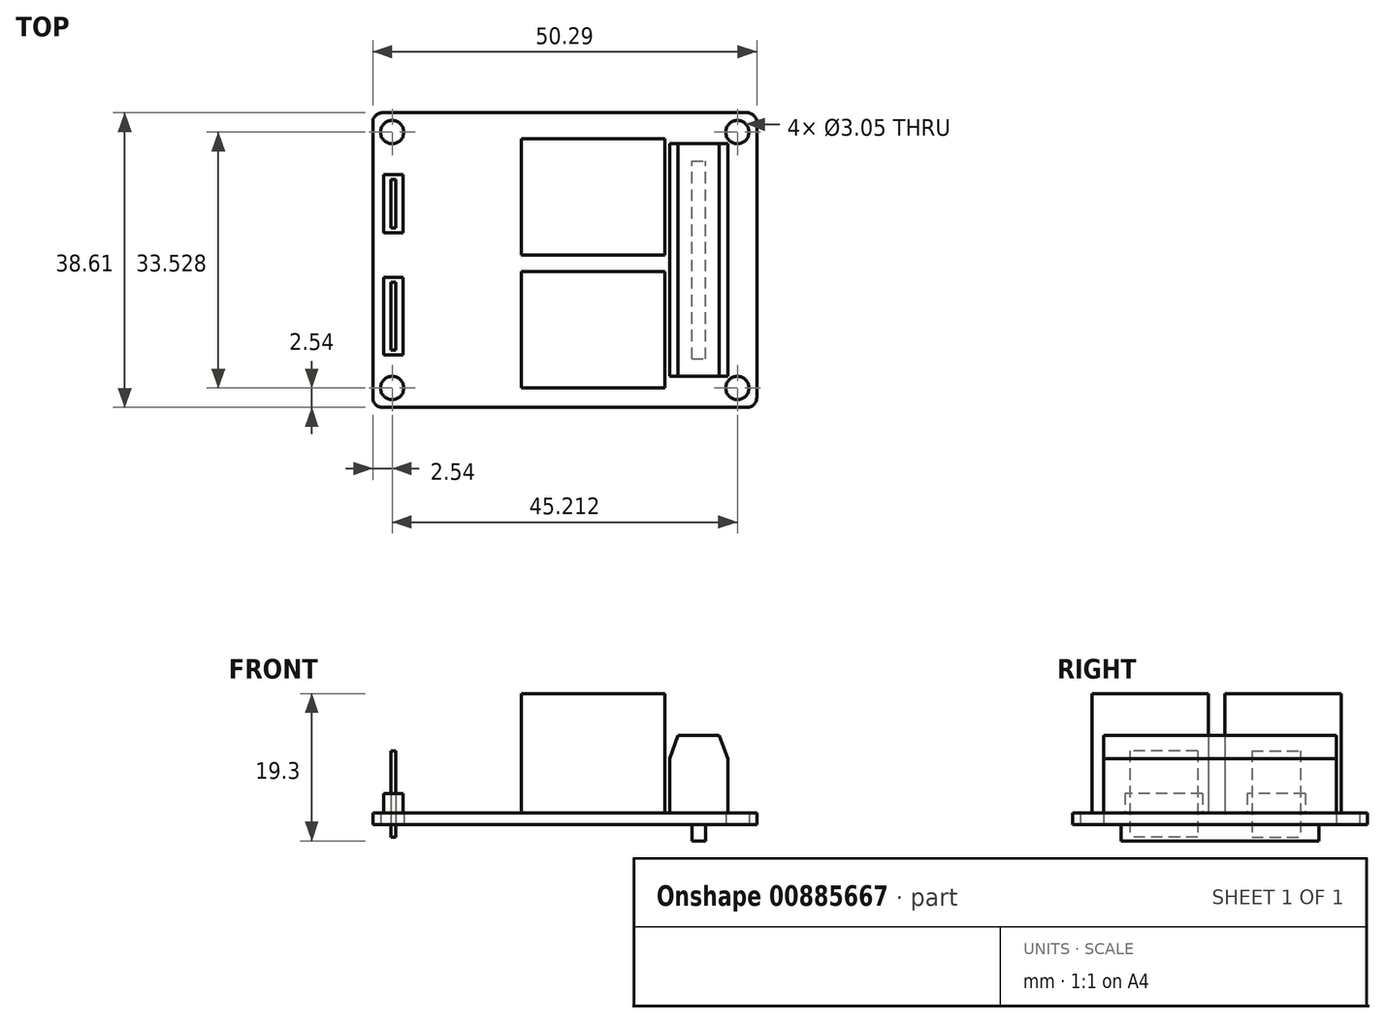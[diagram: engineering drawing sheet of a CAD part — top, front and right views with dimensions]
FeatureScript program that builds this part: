
annotation { "Feature Type Name" : "Feature", "Feature Type Description" : "" }
export const myFeature = defineFeature(function(context is Context, id is Id, definition is map)
    precondition{}
    {
        {
            var Q0;
            Q0=qCreatedBy(makeId("Top.planeOp"),FACE);
            var sketch = newSketch(context, id + "F0", { "sketchPlane" : qUnion([Q0])});
            skLineSegment(sketch, "E0.bottom", {"start": v(0, 0) * mm, "end": v(50.3, 0) * mm});
            skLineSegment(sketch, "E0.top", {"start": v(0, 38.6) * mm, "end": v(50.3, 38.6) * mm});
            skLineSegment(sketch, "E0.left", {"start": v(0, 0) * mm, "end": v(0, 38.6) * mm});
            skLineSegment(sketch, "E0.right", {"start": v(50.3, 0) * mm, "end": v(50.3, 38.6) * mm});
            skLineSegment(sketch, "E1", {"start": v(2.54, -3.55) * mm, "end": v(2.54, 40.4) * mm, "construction": true});
            skLineSegment(sketch, "E2", {"start": v(47.75, 40.69) * mm, "end": v(47.75, -3.26) * mm, "construction": true});
            skLineSegment(sketch, "E3", {"start": v(-3, 36.07) * mm, "end": v(53.81, 36.07) * mm, "construction": true});
            skLineSegment(sketch, "E4", {"start": v(-2.7, 2.54) * mm, "end": v(54.11, 2.54) * mm, "construction": true});
            skCircle(sketch, "E5", {"center": v(2.54, 36.07) * mm, "radius": 1.52 * mm});
            skCircle(sketch, "E6", {"center": v(47.75, 36.07) * mm, "radius": 1.52 * mm});
            skCircle(sketch, "E7", {"center": v(47.75, 2.54) * mm, "radius": 1.52 * mm});
            skCircle(sketch, "E8", {"center": v(2.54, 2.54) * mm, "radius": 1.52 * mm});
            skPoint(sketch, "E9.visualSharp", {"position": v(0, 38.6) * mm});
            skLineSegment(sketch, "E9.filletArc", {"start": v(0, 38.6) * mm, "end": v(0, 38.6) * mm});
            skPoint(sketch, "E10.visualSharp", {"position": v(50.3, 38.6) * mm});
            skLineSegment(sketch, "E10.filletArc", {"start": v(50.3, 38.6) * mm, "end": v(50.3, 38.6) * mm});
            skPoint(sketch, "E11.visualSharp", {"position": v(50.3, 0) * mm});
            skLineSegment(sketch, "E11.filletArc", {"start": v(50.3, 0) * mm, "end": v(50.3, 0) * mm});
            skPoint(sketch, "E12.visualSharp", {"position": v(0, 0) * mm});
            skLineSegment(sketch, "E12.filletArc", {"start": v(0, 0) * mm, "end": v(0, 0) * mm});
            skSolve(sketch);
        }
        {
            var Q0;
            Q0=makeQuery(id+"F0.imprint","IMPRINT",FACE,{"disambiguationData":[TD([[makeQuery(id+"F0.imprint","IMPRINT",EDGE,{"derivedFrom":sQuery(id+"F0.wireOp",EDGE,"E0.bottom")}),1.0]])]});
            extrude(context, id + "F1", {"entities" : qUnion([Q0]), "depth" : 1.52 * mm, "offsetDistance" : 25.4 * mm});
        }
        {
            var Q0;
            Q0=makeQuery(id+"F1.opExtrude","SWEPT_EDGE",EDGE,{"disambiguationData":[OSD([sQuery(id+"F0.wireOp",EDGE,"E0.top"),sQuery(id+"F0.wireOp",EDGE,"E0.right")])]});
            var Q1;
            Q1=makeQuery(id+"F1.opExtrude","SWEPT_EDGE",EDGE,{"disambiguationData":[OSD([sQuery(id+"F0.wireOp",EDGE,"E0.top"),sQuery(id+"F0.wireOp",EDGE,"E0.left")])]});
            var Q2;
            Q2=makeQuery(id+"F1.opExtrude","SWEPT_EDGE",EDGE,{"disambiguationData":[OSD([sQuery(id+"F0.wireOp",EDGE,"E0.bottom"),sQuery(id+"F0.wireOp",EDGE,"E0.left")])]});
            var Q3;
            Q3=makeQuery(id+"F1.opExtrude","SWEPT_EDGE",EDGE,{"disambiguationData":[OSD([sQuery(id+"F0.wireOp",EDGE,"E0.bottom"),sQuery(id+"F0.wireOp",EDGE,"E0.right")])]});
            fillet(context, id + "F2", {"entities" : qUnion([Q0, Q1, Q2, Q3]), "radius" : 1.27 * mm, "tangentPropagation" : true, "allowEdgeOverflow" : false});
        }
        {
            var Q0;
            Q0=makeQuery(id+"F1.opExtrude","CAP_FACE",FACE,{"disambiguationData":[OSD([sQuery(id+"F0.wireOp",EDGE,"E0.bottom"),sQuery(id+"F0.wireOp",EDGE,"E0.top"),sQuery(id+"F0.wireOp",EDGE,"E0.left"),sQuery(id+"F0.wireOp",EDGE,"E0.right"),sQuery(id+"F0.wireOp",EDGE,"E5"),sQuery(id+"F0.wireOp",EDGE,"E6"),sQuery(id+"F0.wireOp",EDGE,"E7"),sQuery(id+"F0.wireOp",EDGE,"E8"),sQuery(id+"F0.wireOp",EDGE,"E9.filletArc"),sQuery(id+"F0.wireOp",EDGE,"E10.filletArc"),sQuery(id+"F0.wireOp",EDGE,"E11.filletArc"),sQuery(id+"F0.wireOp",EDGE,"E12.filletArc")])],"isStart":false});
            var sketch = newSketch(context, id + "F3", { "sketchPlane" : qUnion([Q0])});
            skLineSegment(sketch, "E13.bottom", {"start": v(38.86, 34.54) * mm, "end": v(46.48, 34.54) * mm});
            skLineSegment(sketch, "E13.top", {"start": v(38.86, 4.06) * mm, "end": v(46.48, 4.06) * mm});
            skLineSegment(sketch, "E13.left", {"start": v(38.86, 34.54) * mm, "end": v(38.86, 4.06) * mm});
            skLineSegment(sketch, "E13.right", {"start": v(46.48, 34.54) * mm, "end": v(46.48, 4.06) * mm});
            skLineSegment(sketch, "E14.bottom", {"start": v(19.43, 35.18) * mm, "end": v(38.23, 35.18) * mm});
            skLineSegment(sketch, "E14.top", {"start": v(19.43, 19.94) * mm, "end": v(38.23, 19.94) * mm});
            skLineSegment(sketch, "E14.left", {"start": v(19.43, 35.18) * mm, "end": v(19.43, 19.94) * mm});
            skLineSegment(sketch, "E14.right", {"start": v(38.23, 35.18) * mm, "end": v(38.23, 19.94) * mm});
            skLineSegment(sketch, "E15.bottom", {"start": v(19.43, 17.78) * mm, "end": v(38.23, 17.78) * mm});
            skLineSegment(sketch, "E15.top", {"start": v(19.43, 2.54) * mm, "end": v(38.23, 2.54) * mm});
            skLineSegment(sketch, "E15.left", {"start": v(19.43, 17.78) * mm, "end": v(19.43, 2.54) * mm});
            skLineSegment(sketch, "E15.right", {"start": v(38.23, 17.78) * mm, "end": v(38.23, 2.54) * mm});
            skLineSegment(sketch, "E16.bottom", {"start": v(1.4, 17.02) * mm, "end": v(3.94, 17.02) * mm});
            skLineSegment(sketch, "E16.top", {"start": v(1.4, 6.86) * mm, "end": v(3.94, 6.86) * mm});
            skLineSegment(sketch, "E16.left", {"start": v(1.4, 17.02) * mm, "end": v(1.4, 6.86) * mm});
            skLineSegment(sketch, "E16.right", {"start": v(3.94, 17.02) * mm, "end": v(3.94, 6.86) * mm});
            skLineSegment(sketch, "E17.bottom", {"start": v(1.4, 30.48) * mm, "end": v(3.94, 30.48) * mm});
            skLineSegment(sketch, "E17.top", {"start": v(1.4, 22.86) * mm, "end": v(3.94, 22.86) * mm});
            skLineSegment(sketch, "E17.left", {"start": v(1.4, 30.48) * mm, "end": v(1.4, 22.86) * mm});
            skLineSegment(sketch, "E17.right", {"start": v(3.94, 30.48) * mm, "end": v(3.94, 22.86) * mm});
            skSolve(sketch);
        }
        {
            var Q0;
            Q0=makeQuery(id+"F3.imprint","IMPRINT",FACE,{"disambiguationData":[TD([[makeQuery(id+"F3.imprint","IMPRINT",EDGE,{"derivedFrom":sQuery(id+"F3.wireOp",EDGE,"E13.bottom")}),-1.0]])]});
            extrude(context, id + "F4", {"entities" : qUnion([Q0]), "depth" : 10.16 * mm, "offsetDistance" : 25.4 * mm});
        }
        {
            var Q0;
            Q0=makeQuery(id+"F4.opExtrude","CAP_EDGE",EDGE,{"disambiguationData":[OSD([sQuery(id+"F3.wireOp",EDGE,"E13.right")])],"isStart":false});
            var Q1;
            Q1=makeQuery(id+"F4.opExtrude","CAP_EDGE",EDGE,{"disambiguationData":[OSD([sQuery(id+"F3.wireOp",EDGE,"E13.left")])],"isStart":false});
            chamfer(context, id + "F5", {"entities" : qUnion([Q0, Q1]), "chamferType" : ChamferType.OFFSET_ANGLE, "width" : 3.05 * mm, "oppositeDirection" : false, "angle" : 20 * degree, "tangentPropagation" : true});
        }
        {
            var Q0;
            Q0=makeQuery(id+"F3.imprint","IMPRINT",FACE,{"disambiguationData":[TD([[makeQuery(id+"F3.imprint","IMPRINT",EDGE,{"derivedFrom":sQuery(id+"F3.wireOp",EDGE,"E14.bottom")}),-1.0]])]});
            var Q1;
            Q1=makeQuery(id+"F3.imprint","IMPRINT",FACE,{"disambiguationData":[TD([[makeQuery(id+"F3.imprint","IMPRINT",EDGE,{"derivedFrom":sQuery(id+"F3.wireOp",EDGE,"E15.bottom")}),-1.0]])]});
            extrude(context, id + "F6", {"entities" : qUnion([Q0, Q1]), "depth" : 15.62 * mm, "offsetDistance" : 25.4 * mm});
        }
        {
            var Q0;
            Q0=makeQuery(id+"F3.imprint","IMPRINT",FACE,{"disambiguationData":[TD([[makeQuery(id+"F3.imprint","IMPRINT",EDGE,{"derivedFrom":sQuery(id+"F3.wireOp",EDGE,"E17.bottom")}),-1.0]])]});
            var Q1;
            Q1=makeQuery(id+"F3.imprint","IMPRINT",FACE,{"disambiguationData":[TD([[makeQuery(id+"F3.imprint","IMPRINT",EDGE,{"derivedFrom":sQuery(id+"F3.wireOp",EDGE,"E16.bottom")}),-1.0]])]});
            extrude(context, id + "F7", {"entities" : qUnion([Q0, Q1]), "depth" : 2.54 * mm, "offsetDistance" : 25.4 * mm});
        }
        {
            var Q0;
            Q0=makeQuery(id+"F7.opExtrude","CAP_FACE",FACE,{"disambiguationData":[OSD([sQuery(id+"F3.wireOp",EDGE,"E17.bottom"),sQuery(id+"F3.wireOp",EDGE,"E17.top"),sQuery(id+"F3.wireOp",EDGE,"E17.left"),sQuery(id+"F3.wireOp",EDGE,"E17.right")])],"isStart":false});
            var sketch = newSketch(context, id + "F8", { "sketchPlane" : qUnion([Q0])});
            skLineSegment(sketch, "E18", {"start": v(2.67, 9.13) * mm, "end": v(2.67, 30.48) * mm, "construction": true});
            skLineSegment(sketch, "E19", {"start": v(2.67, 9.13) * mm, "end": v(2.67, 5.86) * mm, "construction": true});
            skLineSegment(sketch, "E20.bottom", {"start": v(2.35, 16.38) * mm, "end": v(2.98, 16.38) * mm});
            skLineSegment(sketch, "E20.top", {"start": v(2.35, 7.5) * mm, "end": v(2.98, 7.5) * mm});
            skLineSegment(sketch, "E20.left", {"start": v(2.35, 16.38) * mm, "end": v(2.35, 7.5) * mm});
            skLineSegment(sketch, "E20.right", {"start": v(2.98, 16.38) * mm, "end": v(2.98, 7.5) * mm});
            skPoint(sketch, "E21", {"position": v(2.67, 7.5) * mm});
            skLineSegment(sketch, "E22.bottom", {"start": v(2.98, 23.5) * mm, "end": v(2.35, 23.5) * mm});
            skLineSegment(sketch, "E22.top", {"start": v(2.98, 29.84) * mm, "end": v(2.35, 29.84) * mm});
            skLineSegment(sketch, "E22.left", {"start": v(2.98, 23.5) * mm, "end": v(2.98, 29.84) * mm});
            skLineSegment(sketch, "E22.right", {"start": v(2.35, 23.5) * mm, "end": v(2.35, 29.84) * mm});
            skSolve(sketch);
        }
        {
            var Q0;
            Q0=makeQuery(id+"F8.imprint","IMPRINT",FACE,{"disambiguationData":[TD([[makeQuery(id+"F8.imprint","IMPRINT",EDGE,{"derivedFrom":sQuery(id+"F8.wireOp",EDGE,"E22.bottom")}),-1.0]])]});
            var Q1;
            Q1=makeQuery(id+"F8.imprint","IMPRINT",FACE,{"disambiguationData":[TD([[makeQuery(id+"F8.imprint","IMPRINT",EDGE,{"derivedFrom":sQuery(id+"F8.wireOp",EDGE,"E20.bottom")}),-1.0]])]});
            extrude(context, id + "F9", {"entities" : qUnion([Q0, Q1]), "depth" : 5.6 * mm, "offsetDistance" : 25.4 * mm, "hasSecondDirection" : true, "secondDirectionOppositeDirection" : true, "secondDirectionDepth" : 5.7 * mm});
        }
        {
            var Q0;
            Q0=makeQuery(id+"F1.opExtrude","CAP_FACE",FACE,{"disambiguationData":[OSD([sQuery(id+"F0.wireOp",EDGE,"E0.bottom"),sQuery(id+"F0.wireOp",EDGE,"E0.top"),sQuery(id+"F0.wireOp",EDGE,"E0.left"),sQuery(id+"F0.wireOp",EDGE,"E0.right"),sQuery(id+"F0.wireOp",EDGE,"E5"),sQuery(id+"F0.wireOp",EDGE,"E6"),sQuery(id+"F0.wireOp",EDGE,"E7"),sQuery(id+"F0.wireOp",EDGE,"E8"),sQuery(id+"F0.wireOp",EDGE,"E9.filletArc"),sQuery(id+"F0.wireOp",EDGE,"E10.filletArc"),sQuery(id+"F0.wireOp",EDGE,"E11.filletArc"),sQuery(id+"F0.wireOp",EDGE,"E12.filletArc")])],"isStart":true});
            var sketch = newSketch(context, id + "F10", { "sketchPlane" : qUnion([Q0])});
            skPoint(sketch, "E23.0", {"position": v(42.67, -34.54) * mm});
            skLineSegment(sketch, "E24", {"start": v(42.67, -4.06) * mm, "end": v(42.67, -34.54) * mm, "construction": true});
            skLineSegment(sketch, "E25.bottom", {"start": v(41.78, -6.35) * mm, "end": v(43.56, -6.35) * mm});
            skLineSegment(sketch, "E25.top", {"start": v(41.78, -32.26) * mm, "end": v(43.56, -32.26) * mm});
            skLineSegment(sketch, "E25.left", {"start": v(41.78, -6.35) * mm, "end": v(41.78, -32.26) * mm});
            skLineSegment(sketch, "E25.right", {"start": v(43.56, -6.35) * mm, "end": v(43.56, -32.26) * mm});
            skPoint(sketch, "E26", {"position": v(42.67, -6.35) * mm});
            skSolve(sketch);
        }
        {
            var Q0;
            Q0=makeQuery(id+"F10.imprint","IMPRINT",FACE,{"disambiguationData":[TD([[makeQuery(id+"F10.imprint","IMPRINT",EDGE,{"derivedFrom":sQuery(id+"F10.wireOp",EDGE,"E25.bottom")}),-1.0]])]});
            extrude(context, id + "F11", {"entities" : qUnion([Q0]), "depth" : 2.16 * mm, "offsetDistance" : 25.4 * mm});
        }
    });
